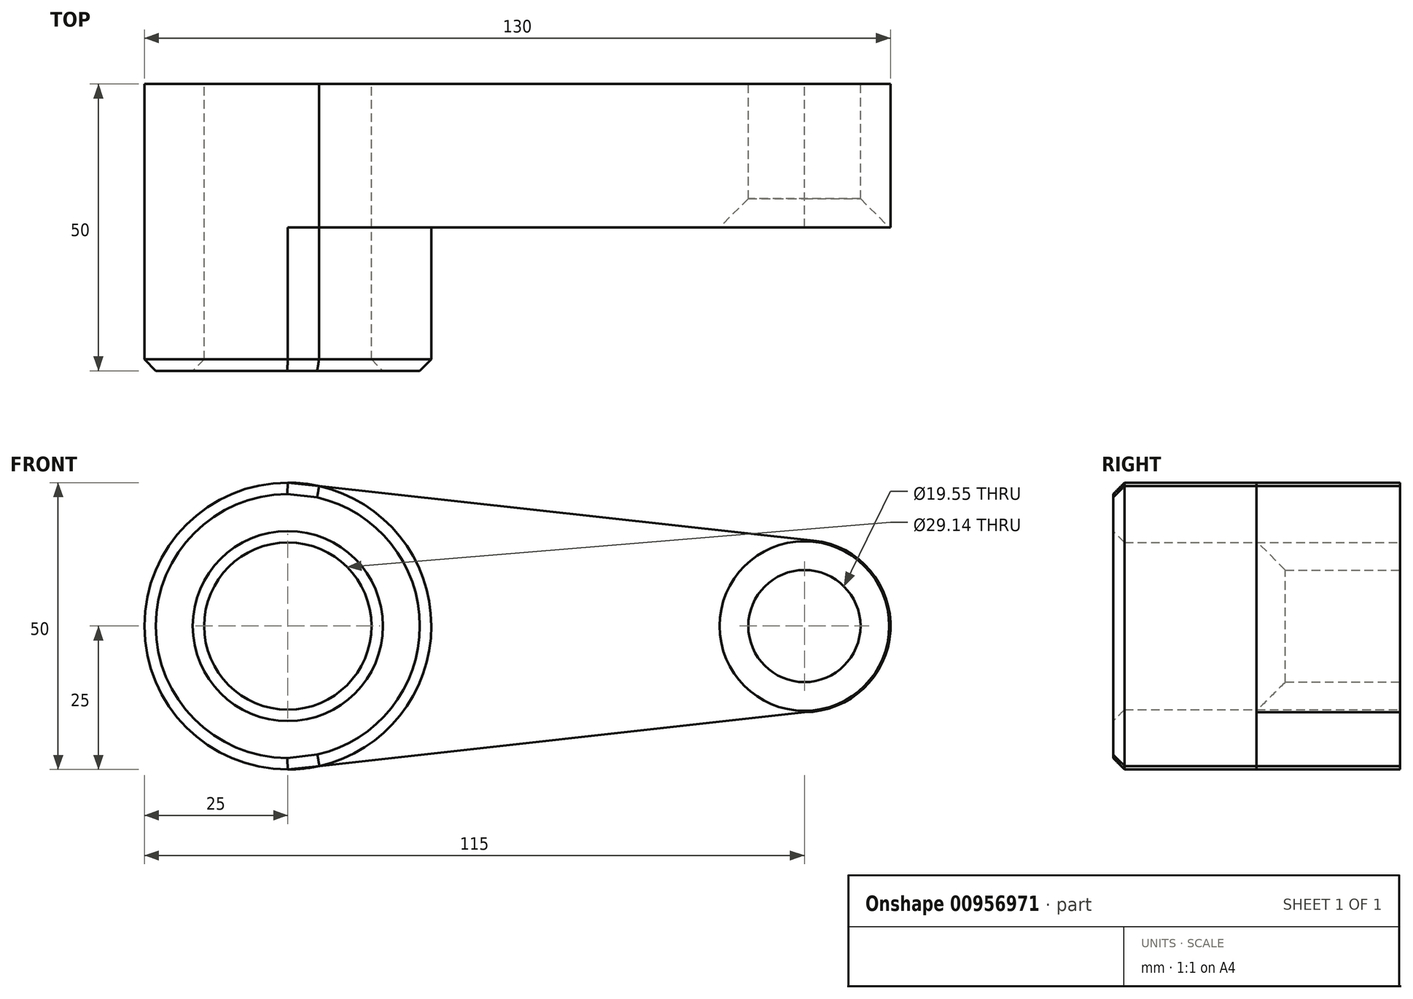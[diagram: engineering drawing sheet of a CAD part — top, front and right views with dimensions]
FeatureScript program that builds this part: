
annotation { "Feature Type Name" : "Feature", "Feature Type Description" : "" }
export const myFeature = defineFeature(function(context is Context, id is Id, definition is map)
    precondition{}
    {
        {
            var Q0;
            Q0=qCreatedBy(makeId("Front.planeOp"),FACE);
            var sketch = newSketch(context, id + "F0", { "sketchPlane" : qUnion([Q0])});
            skCircle(sketch, "E0", {"center": v(0, 0) * mm, "radius": 25 * mm});
            skCircle(sketch, "E1", {"center": v(90, 0) * mm, "radius": 15 * mm});
            skLineSegment(sketch, "E2", {"start": v(0, 25) * mm, "end": v(91.64, 14.9) * mm});
            skLineSegment(sketch, "E3", {"start": v(0, -25) * mm, "end": v(90, -15) * mm});
            skCircle(sketch, "E4", {"center": v(0, 0) * mm, "radius": 14.57 * mm});
            skCircle(sketch, "E5", {"center": v(90, 0) * mm, "radius": 9.78 * mm});
            skSolve(sketch);
        }
        {
            var Q0;
            Q0 = qSketchRegion(id + "F0", true);
            extrude(context, id + "F1", {"entities" : qUnion([Q0]), "depth" : 25 * mm, "offsetDistance" : 25 * mm});
        }
        {
            var Q0;
            Q0=makeQuery(id+"F0.imprint","IMPRINT",FACE,{"disambiguationData":[TD([[makeQuery(id+"F0.imprint","IMPRINT",EDGE,{"derivedFrom":sQuery(id+"F0.wireOp",EDGE,"E4")}),-1.0]])]});
            extrude(context, id + "F2", {"entities" : qUnion([Q0]), "operationType" : NewBodyOperationType.ADD, "depth" : 50 * mm, "offsetDistance" : 25 * mm});
        }
        {
            var Q0;
            Q0=makeQuery(id+"F2.opExtrude","CAP_FACE",FACE,{"disambiguationData":[OSD([sQuery(id+"F0.wireOp",EDGE,"E0"),sQuery(id+"F0.wireOp",EDGE,"E2"),sQuery(id+"F0.wireOp",EDGE,"E3"),sQuery(id+"F0.wireOp",EDGE,"E4")])],"isStart":false});
            chamfer(context, id + "F3", {"entities" : qUnion([Q0]), "width" : 2 * mm, "tangentPropagation" : true});
        }
        {
            var Q0;
            Q0=makeQuery(id+"F1.opExtrude","CAP_EDGE",EDGE,{"disambiguationData":[OSD([sQuery(id+"F0.wireOp",EDGE,"E5")])],"isStart":false});
            chamfer(context, id + "F4", {"entities" : qUnion([Q0]), "width" : 5 * mm, "tangentPropagation" : true});
        }
    });
